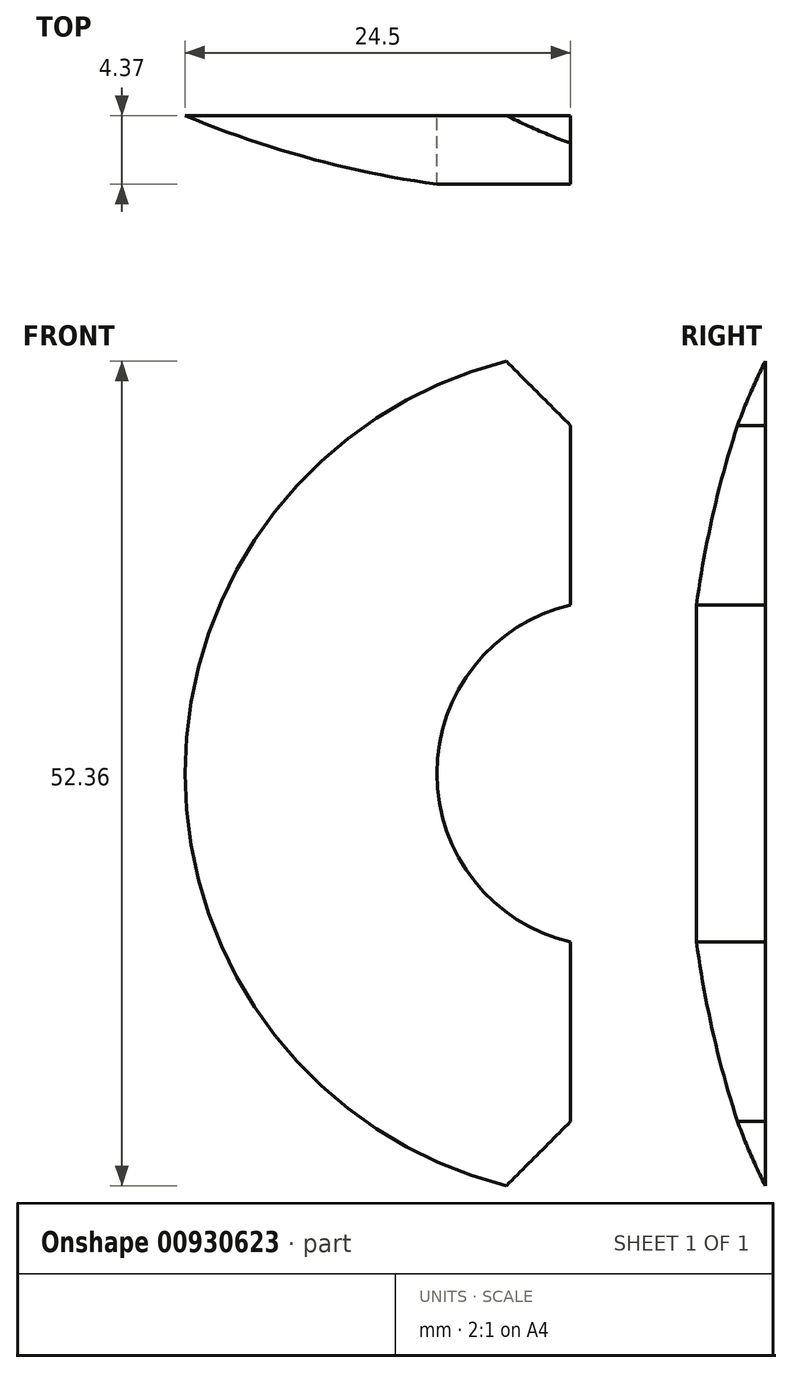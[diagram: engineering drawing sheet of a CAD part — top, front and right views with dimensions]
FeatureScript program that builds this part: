
annotation { "Feature Type Name" : "Feature", "Feature Type Description" : "" }
export const myFeature = defineFeature(function(context is Context, id is Id, definition is map)
    precondition{}
    {
        {
            var Q0;
            Q0=qCreatedBy(makeId("Front.planeOp"),FACE);
            var sketch = newSketch(context, id + "F0", { "sketchPlane" : qUnion([Q0])});
            skArc(sketch, "E0", {"start": v(-6.01, 26.32) * mm, "mid": v(-27, 0) * mm, "end": v(-6.01, -26.32) * mm, "construction": true});
            skArc(sketch, "E1", {"start": v(-2, 10.3) * mm, "mid": v(-10.5, 0) * mm, "end": v(-2, -10.3) * mm, "construction": true});
            skLineSegment(sketch, "E2", {"start": v(-2, 22.3) * mm, "end": v(-2, 10.3) * mm, "construction": true});
            skLineSegment(sketch, "E3", {"start": v(2, 22.3) * mm, "end": v(2, 10.3) * mm, "construction": true});
            skLineSegment(sketch, "E4", {"start": v(-2, 22.3) * mm, "end": v(-6.01, 26.32) * mm, "construction": true});
            skLineSegment(sketch, "E5", {"start": v(2, 22.3) * mm, "end": v(6.01, 26.32) * mm, "construction": true});
            skLineSegment(sketch, "E6", {"start": v(-2, -22.3) * mm, "end": v(-6.01, -26.32) * mm, "construction": true});
            skLineSegment(sketch, "E7", {"start": v(2, -22.3) * mm, "end": v(6.01, -26.32) * mm, "construction": true});
            skLineSegment(sketch, "E8.trimOffspring", {"start": v(-2, -10.3) * mm, "end": v(-2, -22.3) * mm, "construction": true});
            skLineSegment(sketch, "E9.trimOffspring", {"start": v(2, -10.3) * mm, "end": v(2, -22.3) * mm, "construction": true});
            skArc(sketch, "E10.trimOffspring", {"start": v(2, -10.3) * mm, "mid": v(10.5, 0) * mm, "end": v(2, 10.3) * mm, "construction": true});
            skArc(sketch, "E11.trimOffspring", {"start": v(6.01, -26.32) * mm, "mid": v(27, 0) * mm, "end": v(6.01, 26.32) * mm, "construction": true});
            skSolve(sketch);
        }
        {
            var Q0;
            Q0=qCreatedBy(makeId("Front.planeOp"),FACE);
            var sketch = newSketch(context, id + "F1", { "sketchPlane" : qUnion([Q0])});
            skArc(sketch, "E12", {"start": v(-2.5, 10.71) * mm, "mid": v(-11, 0) * mm, "end": v(-2.5, -10.71) * mm});
            skLineSegment(sketch, "E13", {"start": v(-2.5, 10.71) * mm, "end": v(-2.5, 22.1) * mm});
            skLineSegment(sketch, "E14", {"start": v(-2.5, 22.1) * mm, "end": v(-6.58, 26.18) * mm});
            skLineSegment(sketch, "E15", {"start": v(-2.5, -10.71) * mm, "end": v(-2.5, -22.1) * mm});
            skLineSegment(sketch, "E16", {"start": v(-2.5, -22.1) * mm, "end": v(-6.58, -26.18) * mm});
            skArc(sketch, "E17", {"start": v(-6.58, 26.18) * mm, "mid": v(-27, 0) * mm, "end": v(-6.58, -26.18) * mm});
            skSolve(sketch);
        }
        {
            var Q0;
            Q0=qSketchRegion(id+"F1",true);
            extrude(context, id + "F2", {"entities" : qUnion([Q0]), "depth" : 5 * mm, "offsetDistance" : 25 * mm});
        }
        {
            var Q0;
            Q0=qCreatedBy(makeId("Top.planeOp"),FACE);
            var sketch = newSketch(context, id + "F3", { "sketchPlane" : qUnion([Q0])});
            skLineSegment(sketch, "E18", {"start": v(0, 0) * mm, "end": v(0, -5) * mm, "construction": true});
            skLineSegment(sketch, "E19", {"start": v(0, -5) * mm, "end": v(-2, -5) * mm, "construction": true});
            skLineSegment(sketch, "E20", {"start": v(-2, -5) * mm, "end": v(-27, -5) * mm});
            skLineSegment(sketch, "E21", {"start": v(-27, -5) * mm, "end": v(-27, 0) * mm});
            skArc(sketch, "E22", {"start": v(-27, 0) * mm, "mid": v(-14.75, -3.74) * mm, "end": v(-2, -5) * mm});
            skSolve(sketch);
        }
        {
            var Q0;
            Q0=qSketchRegion(id+"F3",true);
            var Q1;
            Q1=sQuery(id+"F3.wireOp",EDGE,"E18");
            revolve(context, id + "F4", {"operationType" : NewBodyOperationType.REMOVE, "surfaceOperationType" : NewSurfaceOperationType.NEW, "entities" : qUnion([Q0]), "axis" : qUnion([Q1]), "revolveType" : RevolveType.FULL, "oppositeDirection" : true});
        }
    });
